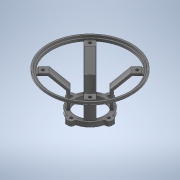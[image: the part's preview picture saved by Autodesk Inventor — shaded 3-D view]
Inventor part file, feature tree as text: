
AUTODESK INVENTOR PART (.ipt)
format: ipt  version: 2020 (Build 240168000, 168)  size: 479,744 bytes
history: native  units: mm
features: other x11, sketch x8, revolve x4, extrude x3, projected_geometry x3, pattern_circular x1, fillet x1
ambient origin geometry x8: Origin, YZ Plane, XZ Plane, XY Plane, X Axis, Y Axis, Z Axis, Center Point
bodies: Body1 (feature_tree)
feature tree (31):
  other  "Твердое тело1"
  extrude  "Выдавливание1"  Depth=34.0mm
  other  "РабПлоскость1"
  other  "РабОсь1"
  revolve  "Вращение1"
  sketch  "Эскиз3"
  other  "РабТочка1"
  extrude  "Выдавливание2"  Depth=45.0mm
  other  "РабТочка2"
  other  "РабТочка3"
  other  "РабТочка4"
  other  "РабПлоскость2"
  sketch  "Эскиз5"
  revolve  "Вращение2"
  revolve  "Вращение3"
  pattern_circular  "Круговой массив1"  Angle=45.0deg  [1 undecoded]
  extrude  "Выдавливание3"  Depth=3.3mm
  revolve  "Вращение4"
  sketch  "Эскиз8"
  fillet  "Сопряжение1"  Radius=9.0mm
  sketch  "Эскиз1"
  sketch  "Эскиз2"
  sketch  "Эскиз4"
  projected_geometry  "Спроецированная петля1"
  projected_geometry  "Спроецированная петля2"
  projected_geometry  "Спроецированная петля3"
  other  "РабПлоскость3"
  other  "РабПлоскость4"
  other  "РабПлоскость5"
  sketch  "Эскиз6"
  sketch  "Эскиз7"
note: 1 required parameter value undecoded (feature->parameter linkage not recoverable at this tier; creation-order binding heuristic only, values carry confidence <= 0.55)
